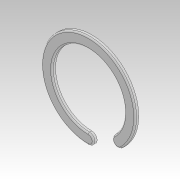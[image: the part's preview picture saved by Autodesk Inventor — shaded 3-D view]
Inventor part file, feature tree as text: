
AUTODESK INVENTOR PART (.ipt)
format: ipt  version: 2020 (Build 240168000, 168)  size: 166,400 bytes
history: native  units: mm
features: other x3, extrude x2, sketch x2, fillet x1, projected_geometry x1
ambient origin geometry x8: Origin, YZ Plane, XZ Plane, XY Plane, X Axis, Y Axis, Z Axis, Center Point
bodies: Solid1 (feature_tree)
feature tree (9):
  other  "Blocks"
  extrude  "Extrusion1"  Depth=0.15mm
  extrude  "Extrusion2"  Depth=1.0mm TaperAngle=360.0deg
  fillet  "Fillet1"  Radius=2.0mm
  sketch  "Sketch1"  dims[d0=8.0mm d1=0.15mm]
  other  "Block1"
  sketch  "Sketch2"  dims[d2=5.8mm d3=80.0mm d5=360.0deg d7=2.0mm d8=0.0mm d9=0.6mm d10=0.0mm d11=1.0mm]
  projected_geometry  "Projected Loop1"
  other  "Block1:1"
